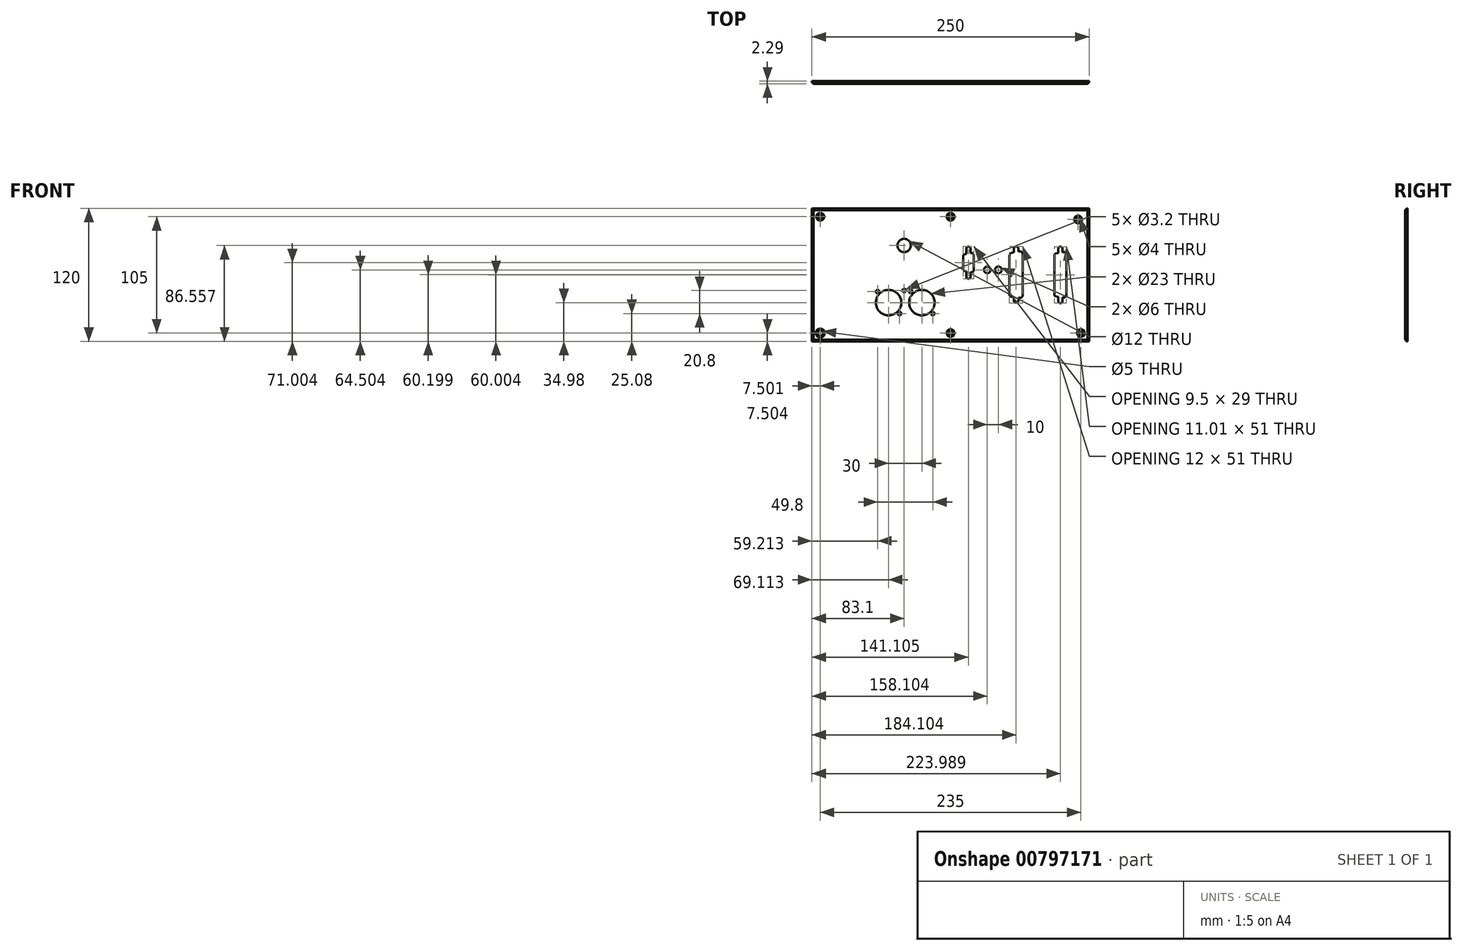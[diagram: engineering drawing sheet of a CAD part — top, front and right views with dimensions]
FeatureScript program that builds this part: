
annotation { "Feature Type Name" : "Feature", "Feature Type Description" : "" }
export const myFeature = defineFeature(function(context is Context, id is Id, definition is map)
    precondition{}
    {
        {
            var Q0;
            Q0=qCreatedBy(makeId("Front.planeOp"),FACE);
            var sketch = newSketch(context, id + "F0", { "sketchPlane" : qUnion([Q0])});
            skLineSegment(sketch, "E0.bottom", {"start": v(-117.07, 74.12) * mm, "end": v(132.93, 74.12) * mm});
            skLineSegment(sketch, "E0.top", {"start": v(-117.07, -45.88) * mm, "end": v(132.93, -45.88) * mm});
            skLineSegment(sketch, "E0.left", {"start": v(-117.07, 74.12) * mm, "end": v(-117.07, -45.88) * mm});
            skLineSegment(sketch, "E0.right", {"start": v(132.93, 74.12) * mm, "end": v(132.93, -45.88) * mm});
            skArc(sketch, "E1", {"start": v(104.98, -9.38) * mm, "mid": v(106.98, -11.38) * mm, "end": v(108.98, -9.38) * mm});
            skArc(sketch, "E2", {"start": v(108.89, 37.62) * mm, "mid": v(106.89, 39.62) * mm, "end": v(104.89, 37.62) * mm});
            skPoint(sketch, "E3.visualSharp", {"position": v(114.16, 32.12) * mm});
            skPoint(sketch, "E4.visualSharp", {"position": v(101.94, -5.68) * mm});
            skPoint(sketch, "E5.visualSharp", {"position": v(111.98, -5.7) * mm});
            skArc(sketch, "E6", {"start": v(65.03, -9.18) * mm, "mid": v(67.03, -11.18) * mm, "end": v(69.03, -9.18) * mm});
            skArc(sketch, "E7", {"start": v(69.03, 37.85) * mm, "mid": v(67, 39.82) * mm, "end": v(65.03, 37.8) * mm});
            skPoint(sketch, "E8.visualSharp", {"position": v(72.03, 34.32) * mm});
            skPoint(sketch, "E9.visualSharp", {"position": v(62.03, 34.32) * mm});
            skPoint(sketch, "E10.visualSharp", {"position": v(61.94, -5.68) * mm});
            skPoint(sketch, "E11.visualSharp", {"position": v(72.03, -5.68) * mm});
            skCircle(sketch, "E12", {"center": v(-17.96, -10.9) * mm, "radius": 11.5 * mm});
            skCircle(sketch, "E13", {"center": v(-8.06, -20.8) * mm, "radius": 1.6 * mm});
            skCircle(sketch, "E14", {"center": v(-27.86, -1) * mm, "radius": 1.6 * mm});
            skCircle(sketch, "E15", {"center": v(-47.96, -10.9) * mm, "radius": 11.5 * mm});
            skCircle(sketch, "E16", {"center": v(-38.06, -20.8) * mm, "radius": 1.6 * mm});
            skCircle(sketch, "E17", {"center": v(-57.86, -1) * mm, "radius": 1.6 * mm});
            skCircle(sketch, "E18", {"center": v(-33.86, 0) * mm, "radius": 1.6 * mm});
            skCircle(sketch, "E19", {"center": v(-33.97, 40.68) * mm, "radius": 6 * mm});
            skLineSegment(sketch, "E20", {"start": v(28.78, 32.31) * mm, "end": v(28.78, 17.94) * mm});
            skLineSegment(sketch, "E21", {"start": v(26.5, 16.46) * mm, "end": v(26.03, 16.55) * mm});
            skLineSegment(sketch, "E22", {"start": v(21.25, 32.88) * mm, "end": v(22.03, 33.02) * mm});
            skPoint(sketch, "E23.visualSharp", {"position": v(28.28, 34.12) * mm});
            skPoint(sketch, "E24.visualSharp", {"position": v(28.28, 16.12) * mm});
            skPoint(sketch, "E25.visualSharp", {"position": v(19.78, 32.62) * mm});
            skLineSegment(sketch, "E26.0", {"start": v(61.03, 31.32) * mm, "end": v(61.03, -2.68) * mm});
            skLineSegment(sketch, "E27.0", {"start": v(69.85, 35.3) * mm, "end": v(69.07, 35.16) * mm});
            skLineSegment(sketch, "E28.0", {"start": v(73.03, 32.32) * mm, "end": v(73.03, -3.68) * mm});
            skLineSegment(sketch, "E29.0", {"start": v(69.87, -6.67) * mm, "end": v(69.03, -6.53) * mm});
            skArc(sketch, "E30", {"start": v(61.03, -3.68) * mm, "mid": v(61.6, -5.01) * mm, "end": v(62.97, -5.52) * mm});
            skArc(sketch, "E31", {"start": v(62.87, 34) * mm, "mid": v(61.54, 32.95) * mm, "end": v(61.03, 31.32) * mm});
            skArc(sketch, "E32", {"start": v(73.03, 32.32) * mm, "mid": v(72.2, 34.62) * mm, "end": v(69.85, 35.3) * mm});
            skLineSegment(sketch, "E33", {"start": v(69.03, 37.85) * mm, "end": v(69.07, 35.16) * mm});
            skLineSegment(sketch, "E34", {"start": v(65.03, -9.18) * mm, "end": v(65.03, -5.87) * mm});
            skLineSegment(sketch, "E35", {"start": v(69.03, -9.18) * mm, "end": v(69.03, -6.53) * mm});
            skLineSegment(sketch, "E36", {"start": v(104.89, 37.62) * mm, "end": v(104.89, 34.21) * mm});
            skLineSegment(sketch, "E37", {"start": v(108.89, 37.62) * mm, "end": v(108.89, 34.96) * mm});
            skArc(sketch, "E38", {"start": v(26.03, 37.62) * mm, "mid": v(24.03, 39.62) * mm, "end": v(22.03, 37.62) * mm});
            skArc(sketch, "E39", {"start": v(22.03, 12.62) * mm, "mid": v(24.03, 10.62) * mm, "end": v(26.03, 12.62) * mm});
            skLineSegment(sketch, "E40", {"start": v(19.28, 31.38) * mm, "end": v(19.28, 19.38) * mm});
            skLineSegment(sketch, "E41", {"start": v(22.03, 37.62) * mm, "end": v(22.03, 33.02) * mm});
            skLineSegment(sketch, "E42", {"start": v(22.03, 12.62) * mm, "end": v(22.03, 17.32) * mm});
            skLineSegment(sketch, "E43", {"start": v(26.03, 12.62) * mm, "end": v(26.03, 16.55) * mm});
            skArc(sketch, "E44", {"start": v(69.87, -6.67) * mm, "mid": v(72.2, -5.96) * mm, "end": v(73.03, -3.68) * mm});
            skCircle(sketch, "E45", {"center": v(41.03, 18.62) * mm, "radius": 3 * mm});
            skCircle(sketch, "E46", {"center": v(51.03, 18.62) * mm, "radius": 3 * mm});
            skCircle(sketch, "E47", {"center": v(-109.57, 66.62) * mm, "radius": 2 * mm});
            skCircle(sketch, "E48", {"center": v(122.93, 64.12) * mm, "radius": 2 * mm});
            skCircle(sketch, "E49", {"center": v(7.93, 66.62) * mm, "radius": 2 * mm});
            skCircle(sketch, "E50", {"center": v(-109.57, -38.38) * mm, "radius": 2.5 * mm});
            skCircle(sketch, "E51", {"center": v(7.93, -38.38) * mm, "radius": 2 * mm});
            skCircle(sketch, "E52", {"center": v(125.43, -38.38) * mm, "radius": 2 * mm});
            skLineSegment(sketch, "E53", {"start": v(26.03, 37.62) * mm, "end": v(26.03, 33.73) * mm});
            skLineSegment(sketch, "E54.trimOffspring", {"start": v(26.03, 33.73) * mm, "end": v(26.51, 33.81) * mm});
            skLineSegment(sketch, "E55.trimOffspring", {"start": v(22.03, 17.32) * mm, "end": v(20.79, 17.55) * mm});
            skLineSegment(sketch, "E56.trimOffspring", {"start": v(65.03, 34.4) * mm, "end": v(62.87, 34) * mm});
            skLineSegment(sketch, "E57.trimOffspring", {"start": v(65.03, -5.87) * mm, "end": v(62.97, -5.52) * mm});
            skLineSegment(sketch, "E58", {"start": v(108.98, -9.38) * mm, "end": v(108.98, -6.73) * mm});
            skLineSegment(sketch, "E59", {"start": v(104.98, -9.38) * mm, "end": v(104.98, -6.06) * mm});
            skLineSegment(sketch, "E60", {"start": v(65.03, 37.8) * mm, "end": v(65.03, 34.4) * mm});
            skLineSegment(sketch, "E61", {"start": v(61.03, -2.68) * mm, "end": v(61.03, -3.68) * mm});
            skArc(sketch, "E62", {"start": v(21.25, 32.88) * mm, "mid": v(20.09, 32.37) * mm, "end": v(19.28, 31.38) * mm});
            skArc(sketch, "E63", {"start": v(28.78, 32.31) * mm, "mid": v(27.95, 33.51) * mm, "end": v(26.51, 33.81) * mm});
            skArc(sketch, "E64", {"start": v(26.5, 16.46) * mm, "mid": v(27.94, 16.74) * mm, "end": v(28.78, 17.94) * mm});
            skArc(sketch, "E65", {"start": v(19.28, 19.38) * mm, "mid": v(19.7, 18.2) * mm, "end": v(20.79, 17.55) * mm});
            skLineSegment(sketch, "E66.0", {"start": v(104.89, 33.72) * mm, "end": v(102.72, 33.31) * mm});
            skLineSegment(sketch, "E67.0", {"start": v(101.41, 30.74) * mm, "end": v(101.42, -3.28) * mm});
            skLineSegment(sketch, "E68.0", {"start": v(112.41, 32.12) * mm, "end": v(112.42, -3.88) * mm});
            skLineSegment(sketch, "E69.0", {"start": v(109.82, 34.62) * mm, "end": v(108.89, 34.44) * mm});
            skLineSegment(sketch, "E70.0", {"start": v(109.84, -6.37) * mm, "end": v(108.98, -6.23) * mm});
            skLineSegment(sketch, "E71.0", {"start": v(104.98, -5.56) * mm, "end": v(102.94, -5.22) * mm});
            skArc(sketch, "E72", {"start": v(101.42, -3.28) * mm, "mid": v(101.8, -4.55) * mm, "end": v(102.94, -5.22) * mm});
            skArc(sketch, "E73", {"start": v(109.84, -6.37) * mm, "mid": v(111.66, -5.67) * mm, "end": v(112.42, -3.88) * mm});
            skArc(sketch, "E74", {"start": v(112.41, 32.12) * mm, "mid": v(111.76, 34.04) * mm, "end": v(109.82, 34.62) * mm});
            skLineSegment(sketch, "E75", {"start": v(104.89, 34.21) * mm, "end": v(104.89, 33.72) * mm});
            skLineSegment(sketch, "E76", {"start": v(104.98, -5.56) * mm, "end": v(104.98, -6.06) * mm});
            skLineSegment(sketch, "E77", {"start": v(108.98, -6.23) * mm, "end": v(108.98, -6.73) * mm});
            skPoint(sketch, "E78.0.end.orphan", {"position": v(112.98, -3.88) * mm});
            skPoint(sketch, "E79.end.orphan", {"position": v(100.98, -3.28) * mm});
            skPoint(sketch, "E80.orphan", {"position": v(104.89, 33.12) * mm});
            skPoint(sketch, "E81.end.orphan", {"position": v(108.89, 33.72) * mm});
            skLineSegment(sketch, "E82", {"start": v(108.89, 34.96) * mm, "end": v(108.89, 34.44) * mm});
            skPoint(sketch, "E83.orphan", {"position": v(104.89, 33.72) * mm});
            skPoint(sketch, "E84.0.start.orphan", {"position": v(112.93, 32.12) * mm});
            skLineSegment(sketch, "E85", {"start": v(101.41, 30.74) * mm, "end": v(101.41, 31.56) * mm});
            skArc(sketch, "E86", {"start": v(102.72, 33.31) * mm, "mid": v(101.77, 32.65) * mm, "end": v(101.41, 31.56) * mm});
            skSolve(sketch);
        }
        {
            var Q0;
            Q0=makeQuery(id+"F0.imprint","IMPRINT",FACE,{"disambiguationData":[TD([[makeQuery(id+"F0.imprint","IMPRINT",EDGE,{"derivedFrom":sQuery(id+"F0.wireOp",EDGE,"E0.bottom")}),-1.0]])]});
            extrude(context, id + "F1", {"entities" : qUnion([Q0]), "depth" : 2.3 * mm, "offsetDistance" : 25 * mm});
        }
        {
            var Q0;
            Q0=makeQuery(id+"F1.opExtrude","CAP_EDGE",EDGE,{"disambiguationData":[OSD([sQuery(id+"F0.wireOp",EDGE,"E0.left")])],"isStart":false});
            var Q1;
            Q1=makeQuery(id+"F1.opExtrude","CAP_EDGE",EDGE,{"disambiguationData":[OSD([sQuery(id+"F0.wireOp",EDGE,"E0.top")])],"isStart":false});
            var Q2;
            Q2=makeQuery(id+"F1.opExtrude","CAP_EDGE",EDGE,{"disambiguationData":[OSD([sQuery(id+"F0.wireOp",EDGE,"E0.right")])],"isStart":false});
            var Q3;
            Q3=makeQuery(id+"F1.opExtrude","CAP_EDGE",EDGE,{"disambiguationData":[OSD([sQuery(id+"F0.wireOp",EDGE,"E0.bottom")])],"isStart":false});
            chamfer(context, id + "F2", {"entities" : qUnion([Q0, Q1, Q2, Q3]), "width" : 1.5 * mm, "tangentPropagation" : true});
        }
        {
            var Q0;
            Q0=makeQuery(id+"F1.opExtrude","CAP_EDGE",EDGE,{"disambiguationData":[OSD([sQuery(id+"F0.wireOp",EDGE,"E47")])],"isStart":false});
            var Q1;
            Q1=makeQuery(id+"F1.opExtrude","CAP_EDGE",EDGE,{"disambiguationData":[OSD([sQuery(id+"F0.wireOp",EDGE,"E49")])],"isStart":false});
            var Q2;
            Q2=makeQuery(id+"F1.opExtrude","CAP_EDGE",EDGE,{"disambiguationData":[OSD([sQuery(id+"F0.wireOp",EDGE,"E48")])],"isStart":false});
            var Q3;
            Q3=makeQuery(id+"F1.opExtrude","CAP_EDGE",EDGE,{"disambiguationData":[OSD([sQuery(id+"F0.wireOp",EDGE,"E52")])],"isStart":false});
            var Q4;
            Q4=makeQuery(id+"F1.opExtrude","CAP_EDGE",EDGE,{"disambiguationData":[OSD([sQuery(id+"F0.wireOp",EDGE,"E51")])],"isStart":false});
            var Q5;
            Q5=makeQuery(id+"F1.opExtrude","CAP_EDGE",EDGE,{"disambiguationData":[OSD([sQuery(id+"F0.wireOp",EDGE,"E50")])],"isStart":false});
            chamfer(context, id + "F3", {"entities" : qUnion([Q0, Q1, Q2, Q3, Q4, Q5]), "width" : 1.5 * mm, "tangentPropagation" : true});
        }
    });
